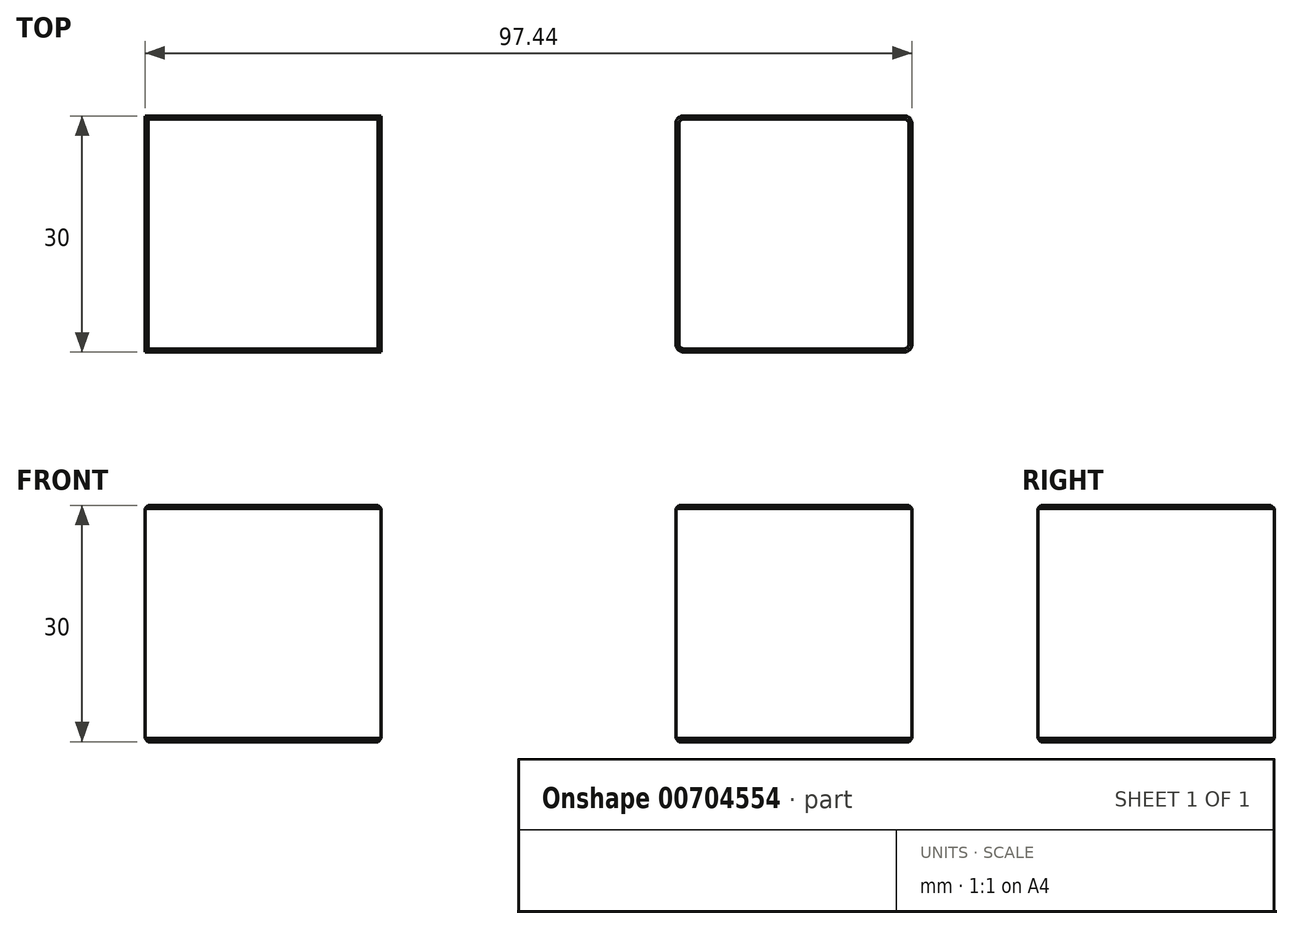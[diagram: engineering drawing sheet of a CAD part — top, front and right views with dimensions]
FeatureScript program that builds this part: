
annotation { "Feature Type Name" : "Feature", "Feature Type Description" : "" }
export const myFeature = defineFeature(function(context is Context, id is Id, definition is map)
    precondition{}
    {
        {
            var Q0;
            Q0=qCreatedBy(makeId("Top.planeOp"),FACE);
            var sketch = newSketch(context, id + "F0", { "sketchPlane" : qUnion([Q0])});
            skLineSegment(sketch, "E0.bottom", {"start": v(-15, -15) * mm, "end": v(15, -15) * mm});
            skLineSegment(sketch, "E0.top", {"start": v(-15, 15) * mm, "end": v(15, 15) * mm});
            skLineSegment(sketch, "E0.left", {"start": v(-15, -15) * mm, "end": v(-15, 15) * mm});
            skLineSegment(sketch, "E0.right", {"start": v(15, -15) * mm, "end": v(15, 15) * mm});
            skPoint(sketch, "E0.middle", {"position": v(0, 0) * mm});
            skLineSegment(sketch, "E1.bottom", {"start": v(52.44, -15) * mm, "end": v(82.44, -15) * mm});
            skLineSegment(sketch, "E1.top", {"start": v(52.44, 15) * mm, "end": v(82.44, 15) * mm});
            skLineSegment(sketch, "E1.left", {"start": v(52.44, -15) * mm, "end": v(52.44, 15) * mm});
            skLineSegment(sketch, "E1.right", {"start": v(82.44, -15) * mm, "end": v(82.44, 15) * mm});
            skPoint(sketch, "E1.middle", {"position": v(67.44, 0) * mm});
            skSolve(sketch);
        }
        {
            var Q0;
            Q0=makeQuery(id+"F0.imprint","IMPRINT",FACE,{"disambiguationData":[TD([[makeQuery(id+"F0.imprint","IMPRINT",EDGE,{"derivedFrom":sQuery(id+"F0.wireOp",EDGE,"E1.bottom")}),1.0]])]});
            var Q1;
            Q1=makeQuery(id+"F0.imprint","IMPRINT",FACE,{"disambiguationData":[TD([[makeQuery(id+"F0.imprint","IMPRINT",EDGE,{"derivedFrom":sQuery(id+"F0.wireOp",EDGE,"E0.bottom")}),1.0]])]});
            extrude(context, id + "F1", {"entities" : qUnion([Q0, Q1]), "depth" : 30 * mm, "offsetDistance" : 25 * mm});
        }
        {
            var Q0;
            Q0=makeQuery(id+"F1.opExtrude","SWEPT_EDGE",EDGE,{"disambiguationData":[OSD([sQuery(id+"F0.wireOp",EDGE,"E1.bottom"),sQuery(id+"F0.wireOp",EDGE,"E1.left")])]});
            var Q1;
            Q1=makeQuery(id+"F1.opExtrude","SWEPT_EDGE",EDGE,{"disambiguationData":[OSD([sQuery(id+"F0.wireOp",EDGE,"E1.bottom"),sQuery(id+"F0.wireOp",EDGE,"E1.right")])]});
            var Q2;
            Q2=makeQuery(id+"F1.opExtrude","SWEPT_EDGE",EDGE,{"disambiguationData":[OSD([sQuery(id+"F0.wireOp",EDGE,"E1.top"),sQuery(id+"F0.wireOp",EDGE,"E1.right")])]});
            var Q3;
            Q3=makeQuery(id+"F1.opExtrude","SWEPT_EDGE",EDGE,{"disambiguationData":[OSD([sQuery(id+"F0.wireOp",EDGE,"E1.top"),sQuery(id+"F0.wireOp",EDGE,"E1.left")])]});
            fillet(context, id + "F2", {"entities" : qUnion([Q0, Q1, Q2, Q3]), "radius" : 1 * mm, "tangentPropagation" : true, "allowEdgeOverflow" : false});
        }
        {
            var Q0;
            Q0=makeQuery(id+"F1.opExtrude","CAP_FACE",FACE,{"disambiguationData":[OSD([sQuery(id+"F0.wireOp",EDGE,"E0.bottom"),sQuery(id+"F0.wireOp",EDGE,"E0.top"),sQuery(id+"F0.wireOp",EDGE,"E0.left"),sQuery(id+"F0.wireOp",EDGE,"E0.right")])],"isStart":false});
            var Q1;
            Q1=makeQuery(id+"F1.opExtrude","CAP_FACE",FACE,{"disambiguationData":[OSD([sQuery(id+"F0.wireOp",EDGE,"E1.bottom"),sQuery(id+"F0.wireOp",EDGE,"E1.top"),sQuery(id+"F0.wireOp",EDGE,"E1.left"),sQuery(id+"F0.wireOp",EDGE,"E1.right")])],"isStart":false});
            var Q2;
            Q2=makeQuery(id+"F1.opExtrude","CAP_FACE",FACE,{"disambiguationData":[OSD([sQuery(id+"F0.wireOp",EDGE,"E1.bottom"),sQuery(id+"F0.wireOp",EDGE,"E1.top"),sQuery(id+"F0.wireOp",EDGE,"E1.left"),sQuery(id+"F0.wireOp",EDGE,"E1.right")])],"isStart":true});
            var Q3;
            Q3=makeQuery(id+"F1.opExtrude","CAP_FACE",FACE,{"disambiguationData":[OSD([sQuery(id+"F0.wireOp",EDGE,"E0.bottom"),sQuery(id+"F0.wireOp",EDGE,"E0.top"),sQuery(id+"F0.wireOp",EDGE,"E0.left"),sQuery(id+"F0.wireOp",EDGE,"E0.right")])],"isStart":true});
            chamfer(context, id + "F3", {"entities" : qUnion([Q0, Q1, Q2, Q3]), "width" : 0.4 * mm, "tangentPropagation" : true});
        }
    });
